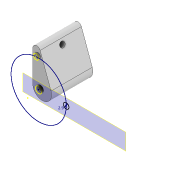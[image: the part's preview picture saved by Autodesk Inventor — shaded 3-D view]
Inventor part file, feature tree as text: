
AUTODESK INVENTOR PART (.ipt)
format: ipt  version: 2022 (Build 260153000, 153)  size: 133,120 bytes
history: native  units: mm
features: sketch x5, extrude x4, projected_geometry x2, other x2, fillet x1, plane x1, reference x1
ambient origin geometry x8: Origin, YZ Plane, XZ Plane, XY Plane, X Axis, Y Axis, Z Axis, Center Point
bodies: Volumenkörper1 (feature_tree)
feature tree (16):
  extrude  "Extrusion1"  Depth=3.0mm
  fillet  "Rundung1"  Radius=1.0mm
  extrude  "Extrusion2"  Depth=22.0mm TaperAngle=0.0deg
  extrude  "Extrusion3"  Depth=2.0mm
  plane  "Arbeitsebene1"
  sketch  "Skizze4"  dims[d8=2.9mm d9=4.0mm d10=0.0mm]
  extrude  "Extrusion4"  Depth=4.0mm TaperAngle=0.0deg
  sketch  "Skizze1"  dims[d0=20.0mm d1=3.0mm d2=1.0mm]
  reference  "Referenz1"
  sketch  "Skizze2"  dims[d3=2.0mm d4=22.0mm d5=0.0mm]
  projected_geometry  "Projizierte Kontur1"
  sketch  "Skizze3"  dims[d6=0.2mm d7=2.0mm]
  sketch  "Skizze5"  dims[d11=4.0mm d12=0.0mm d13=2.9mm d14=10.0mm d15=2.8mm d16=10.0mm d17=0.0mm]
  projected_geometry  "Projizierte Kontur2"
  other  "Anglerfish_lunchbox_m12large_flipped_v0.iam"
  other  "Anglerfish_coverslipclamp_top:1"
